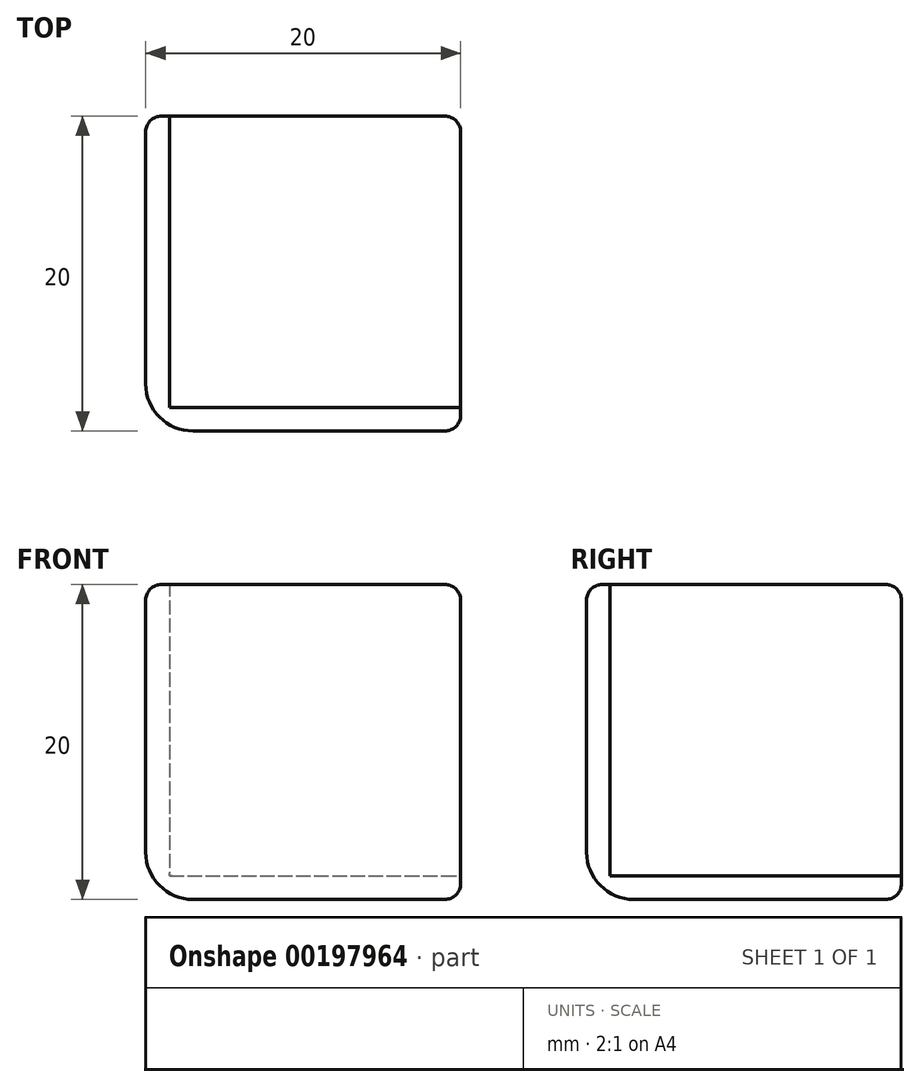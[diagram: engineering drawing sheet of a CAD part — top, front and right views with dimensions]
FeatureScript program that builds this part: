
annotation { "Feature Type Name" : "Feature", "Feature Type Description" : "" }
export const myFeature = defineFeature(function(context is Context, id is Id, definition is map)
    precondition{}
    {
        {
            var Q0;
            Q0=qCreatedBy(makeId("Top.planeOp"),FACE);
            var sketch = newSketch(context, id + "F0", { "sketchPlane" : qUnion([Q0])});
            skLineSegment(sketch, "E0", {"start": v(0, 0) * mm, "end": v(20, 0) * mm});
            skLineSegment(sketch, "E1", {"start": v(20, 0) * mm, "end": v(20, 1.5) * mm});
            skLineSegment(sketch, "E2", {"start": v(20, 1.5) * mm, "end": v(1.5, 1.5) * mm});
            skLineSegment(sketch, "E3", {"start": v(1.5, 1.5) * mm, "end": v(1.5, 20) * mm});
            skLineSegment(sketch, "E4", {"start": v(1.5, 20) * mm, "end": v(0, 20) * mm});
            skLineSegment(sketch, "E5", {"start": v(0, 20) * mm, "end": v(0, 0) * mm});
            skSolve(sketch);
        }
        {
            var Q0;
            Q0 = qSketchRegion(id + "F0", true);
            extrude(context, id + "F1", {"entities" : qUnion([Q0]), "depth" : 20 * mm});
        }
        {
            var Q0;
            Q0=qCreatedBy(makeId("Front.planeOp"),FACE);
            var sketch = newSketch(context, id + "F2", { "sketchPlane" : qUnion([Q0])});
            skLineSegment(sketch, "E6", {"start": v(0, 0) * mm, "end": v(0, 20) * mm});
            skLineSegment(sketch, "E7", {"start": v(0, 20) * mm, "end": v(1.5, 20) * mm});
            skLineSegment(sketch, "E8", {"start": v(1.5, 20) * mm, "end": v(1.5, 1.5) * mm});
            skLineSegment(sketch, "E9", {"start": v(1.5, 1.5) * mm, "end": v(20, 1.5) * mm});
            skLineSegment(sketch, "E10", {"start": v(20, 1.5) * mm, "end": v(20, 0) * mm});
            skLineSegment(sketch, "E11", {"start": v(20, 0) * mm, "end": v(0, 0) * mm});
            skSolve(sketch);
        }
        {
            var Q0;
            Q0 = qSketchRegion(id + "F2", true);
            extrude(context, id + "F3", {"entities" : qUnion([Q0]), "operationType" : NewBodyOperationType.ADD, "oppositeDirection" : true, "depth" : 20 * mm});
        }
        {
            var Q0;
            Q0=makeQuery(id+"F1.opExtrude","SWEPT_EDGE",EDGE,{"disambiguationData":[OSD([sQuery(id+"F0.wireOp",EDGE,"E0"),sQuery(id+"F0.wireOp",EDGE,"E5")])]});
            var Q1;
            Q1=makeQuery(id+"F1.opExtrude","CAP_EDGE",EDGE,{"disambiguationData":[OSD([sQuery(id+"F0.wireOp",EDGE,"E5")])],"isStart":true});
            var Q2;
            Q2=makeQuery(id+"F1.opExtrude","CAP_EDGE",EDGE,{"disambiguationData":[OSD([sQuery(id+"F0.wireOp",EDGE,"E0")])],"isStart":true});
            fillet(context, id + "F4", {"entities" : qUnion([Q0, Q1, Q2]), "radius" : 3 * mm, "tangentPropagation" : true, "allowEdgeOverflow" : false});
        }
        {
            var Q0;
            Q0=makeQuery(id+"F1.opExtrude","CAP_EDGE",EDGE,{"disambiguationData":[OSD([sQuery(id+"F0.wireOp",EDGE,"E5")])],"isStart":false});
            var Q1;
            Q1=makeQuery(id+"F3.boolean.opBoolean","MERGE",EDGE,{"derivedFrom":[makeQuery(id+"F1.opExtrude","CAP_EDGE",EDGE,{"disambiguationData":[OSD([sQuery(id+"F0.wireOp",EDGE,"E1")])],"isStart":true}),makeQuery(id+"F3.opExtrude","SWEPT_EDGE",EDGE,{"disambiguationData":[OSD([sQuery(id+"F2.wireOp",EDGE,"E10"),sQuery(id+"F2.wireOp",EDGE,"E11")])]})]});
            var Q2;
            Q2=makeQuery(id+"F3.boolean.opBoolean","MERGE",EDGE,{"derivedFrom":[makeQuery(id+"F1.opExtrude","CAP_EDGE",EDGE,{"disambiguationData":[OSD([sQuery(id+"F0.wireOp",EDGE,"E4")])],"isStart":true}),makeQuery(id+"F3.opExtrude","CAP_EDGE",EDGE,{"disambiguationData":[OSD([sQuery(id+"F2.wireOp",EDGE,"E11")])],"isStart":false})]});
            var Q3;
            Q3=makeQuery(id+"F1.opExtrude","CAP_EDGE",EDGE,{"disambiguationData":[OSD([sQuery(id+"F0.wireOp",EDGE,"E4")])],"isStart":false});
            var Q4;
            Q4=makeQuery(id+"F3.opExtrude","CAP_EDGE",EDGE,{"disambiguationData":[OSD([sQuery(id+"F2.wireOp",EDGE,"E10")])],"isStart":false});
            var Q5;
            Q5=makeQuery(id+"F1.opExtrude","CAP_EDGE",EDGE,{"disambiguationData":[OSD([sQuery(id+"F0.wireOp",EDGE,"E1")])],"isStart":false});
            fillet(context, id + "F5", {"entities" : qUnion([Q0, Q1, Q2, Q3, Q4, Q5]), "radius" : 1 * mm, "tangentPropagation" : true, "allowEdgeOverflow" : false});
        }
    });
